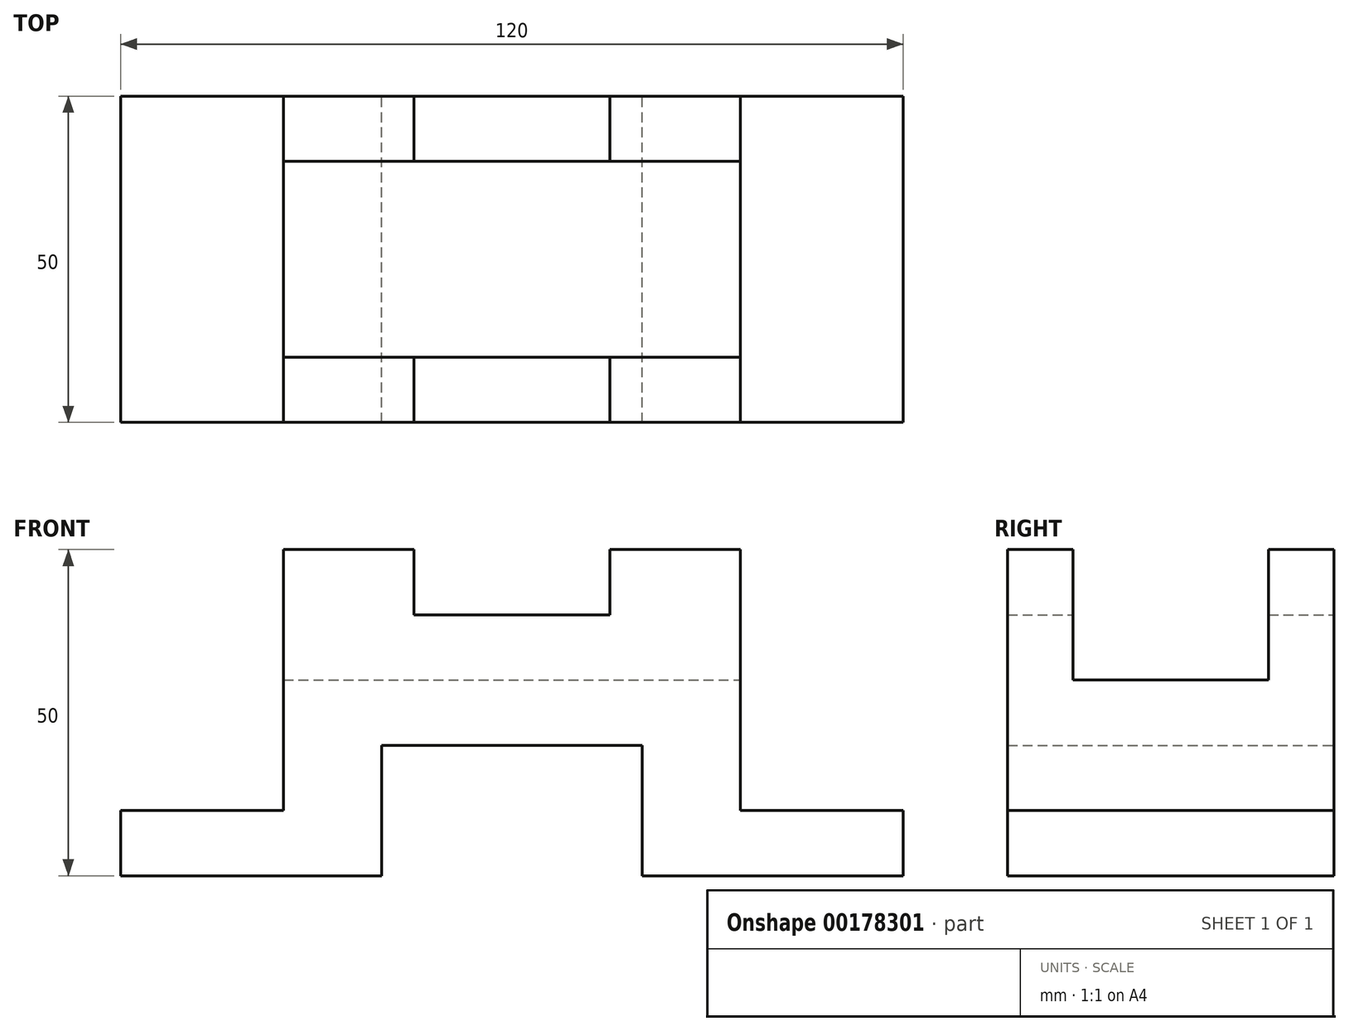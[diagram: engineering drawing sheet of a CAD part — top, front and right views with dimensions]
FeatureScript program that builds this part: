
annotation { "Feature Type Name" : "Feature", "Feature Type Description" : "" }
export const myFeature = defineFeature(function(context is Context, id is Id, definition is map)
    precondition{}
    {
        {
            var Q0;
            Q0=qCreatedBy(makeId("Front.planeOp"),FACE);
            var sketch = newSketch(context, id + "F0", { "sketchPlane" : qUnion([Q0])});
            skLineSegment(sketch, "E0", {"start": v(0, 20) * mm, "end": v(20, 20) * mm});
            skLineSegment(sketch, "E1", {"start": v(20, 20) * mm, "end": v(20, 0) * mm});
            skLineSegment(sketch, "E2", {"start": v(20, 0) * mm, "end": v(60, 0) * mm});
            skLineSegment(sketch, "E3", {"start": v(60, 0) * mm, "end": v(60, 10) * mm});
            skLineSegment(sketch, "E4", {"start": v(60, 10) * mm, "end": v(35, 10) * mm});
            skLineSegment(sketch, "E5", {"start": v(35, 10) * mm, "end": v(35, 50) * mm});
            skLineSegment(sketch, "E6", {"start": v(35, 50) * mm, "end": v(15, 50) * mm});
            skLineSegment(sketch, "E7", {"start": v(0, 20) * mm, "end": v(0, 40) * mm});
            skLineSegment(sketch, "E8", {"start": v(0, 40) * mm, "end": v(15, 40) * mm});
            skLineSegment(sketch, "E9", {"start": v(15, 40) * mm, "end": v(15, 50) * mm});
            skSolve(sketch);
        }
        {
            var Q0;
            Q0=makeQuery(id+"F0.imprint","IMPRINT",FACE,{"disambiguationData":[TD([[makeQuery(id+"F0.imprint","IMPRINT",EDGE,{"derivedFrom":sQuery(id+"F0.wireOp",EDGE,"E0")}),1.0]])]});
            extrude(context, id + "F1", {"entities" : qUnion([Q0]), "endBound" : BoundingType.SYMMETRIC, "depth" : 50 * mm});
        }
        {
            var Q0;
            Q0=makeQuery(id+"F1.opExtrude","SWEPT_FACE",FACE,{"disambiguationData":[OSD([sQuery(id+"F0.wireOp",EDGE,"E5")])]});
            var sketch = newSketch(context, id + "F2", { "sketchPlane" : qUnion([Q0])});
            skLineSegment(sketch, "E10.bottom", {"start": v(15, 50) * mm, "end": v(-15, 50) * mm});
            skLineSegment(sketch, "E10.top", {"start": v(15, 30) * mm, "end": v(-15, 30) * mm});
            skLineSegment(sketch, "E10.left", {"start": v(15, 50) * mm, "end": v(15, 30) * mm});
            skLineSegment(sketch, "E10.right", {"start": v(-15, 50) * mm, "end": v(-15, 30) * mm});
            skLineSegment(sketch, "E11", {"start": v(15, 30) * mm, "end": v(25, 30) * mm, "construction": true});
            skLineSegment(sketch, "E12", {"start": v(-25, 30) * mm, "end": v(-15, 30) * mm, "construction": true});
            skSolve(sketch);
        }
        {
            var Q0;
            Q0 = qSketchRegion(id + "F2", true);
            extrude(context, id + "F3", {"entities" : qUnion([Q0]), "operationType" : NewBodyOperationType.REMOVE, "endBound" : BoundingType.THROUGH_ALL, "oppositeDirection" : true, "depth" : 25 * mm});
        }
        {
            var Q0;
            Q0=makeQuery(id+"F1.opExtrude","SWEPT_BODY",BODY,{"disambiguationData":[OSD([sQuery(id+"F0.wireOp",EDGE,"E0"),sQuery(id+"F0.wireOp",EDGE,"E1"),sQuery(id+"F0.wireOp",EDGE,"E2"),sQuery(id+"F0.wireOp",EDGE,"E3"),sQuery(id+"F0.wireOp",EDGE,"E4"),sQuery(id+"F0.wireOp",EDGE,"E5"),sQuery(id+"F0.wireOp",EDGE,"E6"),sQuery(id+"F0.wireOp",EDGE,"E7"),sQuery(id+"F0.wireOp",EDGE,"E8"),sQuery(id+"F0.wireOp",EDGE,"E9")])]});
            var Q1;
            Q1=qCreatedBy(makeId("Right.planeOp"),FACE);
            mirror(context, id + "F4", {"operationType" : NewBodyOperationType.ADD, "entities" : qUnion([Q0]), "mirrorPlane" : qUnion([Q1])});
        }
    });
